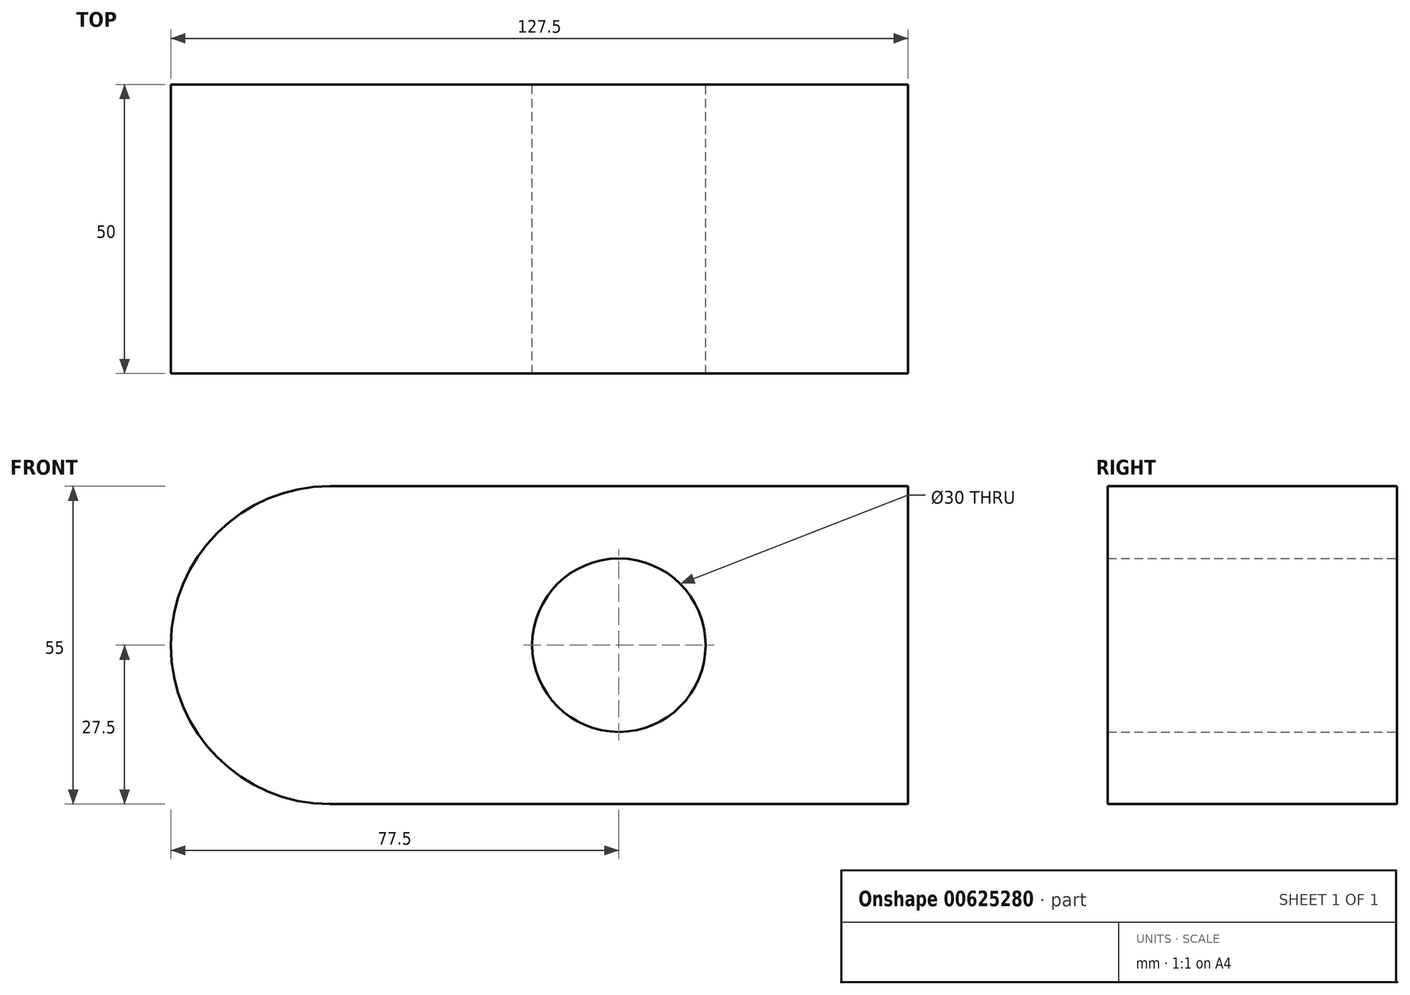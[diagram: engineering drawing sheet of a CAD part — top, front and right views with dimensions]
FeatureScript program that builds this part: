
annotation { "Feature Type Name" : "Feature", "Feature Type Description" : "" }
export const myFeature = defineFeature(function(context is Context, id is Id, definition is map)
    precondition{}
    {
        {
            var Q0;
            Q0=qCreatedBy(makeId("Front.planeOp"),FACE);
            var sketch = newSketch(context, id + "F0", { "sketchPlane" : qUnion([Q0])});
            skLineSegment(sketch, "E0.bottom", {"start": v(0, 0) * mm, "end": v(-100, 0) * mm});
            skLineSegment(sketch, "E0.top", {"start": v(0, 55) * mm, "end": v(-100, 55) * mm});
            skLineSegment(sketch, "E0.left", {"start": v(0, 0) * mm, "end": v(0, 55) * mm});
            skArc(sketch, "E1", {"start": v(-100, 55) * mm, "mid": v(-127.5, 27.5) * mm, "end": v(-100, 0) * mm});
            skCircle(sketch, "E2", {"center": v(-50, 27.5) * mm, "radius": 15 * mm});
            skPoint(sketch, "E2.centerSnap0", {"position": v(-50, 55) * mm});
            skSolve(sketch);
        }
        {
            var Q0;
            Q0 = qSketchRegion(id + "F0", true);
            extrude(context, id + "F1", {"entities" : qUnion([Q0]), "depth" : 50 * mm, "offsetDistance" : 25 * mm});
        }
    });
